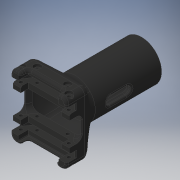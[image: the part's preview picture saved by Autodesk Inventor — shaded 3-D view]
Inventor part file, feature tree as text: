
AUTODESK INVENTOR PART (.ipt)
format: ipt  version: 2019 (Build 230136000, 136)  size: 1,152,512 bytes
history: native  units: in
note: dims shown in document units (in); Inventor stores cm internally (conversion verified against a paired STEP export)
features: extrude x9, sketch x7, chamfer x4, other x3, plane x3, fillet x2, loft x2, shell x1, pattern_circular x1, emboss x1, projected_geometry x1
ambient origin geometry x8: Origin, YZ Plane, XZ Plane, XY Plane, X Axis, Y Axis, Z Axis, Center Point
bodies: Solid3 (feature_tree), Solid1 (feature_tree)
feature tree (34):
  other  "servo holder.ipt"
  plane  "Work Plane2"
  extrude  "Extrusion2"  Depth=0.3937in
  fillet  "Fillet1"  Radius=1.1417in
  plane  "Work Plane1"
  sketch  "Sketch1"  dims[d0=0.3937in d1=2.4283in d2=1.1417in]
  sketch  "Sketch2"  dims[d7=0.9449in d8=0.0787in]
  extrude  "Extrusion8"  Depth=0.0787in
  loft  "Loft2"
  shell  "Shell1"  Thickness=0.0787in
  loft  "Loft3"
  extrude  "Extrusion1"  Depth=0.1969in
  sketch  "Sketch4"  dims[d21=0.0in d22=0.0in d23=0.0689in]
  extrude  "Extrusion3"  Depth=0.7874in TaperAngle=0.0deg
  extrude  "Extrusion4"  Depth=0.2362in TaperAngle=0.0deg
  extrude  "Extrusion5"  Depth=0.1575in
  chamfer  "Chamfer2"  Distance=3.1496in Angle=360.0deg
  pattern_circular  "Circular Pattern1"  [2 undecoded]
  extrude  "Extrusion6"  Depth=0.4331in
  chamfer  "Chamfer1"  Distance=0.1969in Angle=45.0deg
  plane  "Work Plane3"
  sketch  "Sketch5"  dims[d29=0.1102in d35=0.1969in]
  extrude  "Extrusion7"  Depth=0.1575in TaperAngle=45.0deg
  emboss  "Emboss1"
  fillet  "Fillet2"  Radius=0.3937in
  chamfer  "Chamfer3"  Distance=0.4724in
  extrude  "Extrusion9"  Depth=0.2362in
  chamfer  "Chamfer4"  Distance=0.2362in
  other  "Solid1::servo holder.ipt"
  other  "TaggingFeature1"
  sketch  "Sketch3"  dims[d11=0.3937in d12=90.0deg d13=1.1811in d14=90.0deg d15=0.1969in d16=90.0deg d17=0.1575in d18=0.0in d19=2.3622in d20=0.0787in]
  sketch  "Sketch6"  dims[d36=0.9843in d37=-0.0137in d38=0.7874in d39=0.0in]
  sketch  "Sketch7"  dims[d40=0.3937in d42=0.2362in d43=0.0in d44=0.1575in d45=3.1496in d46=360.0deg d48=0.2362in d49=0.0in d50=0.4331in d51=0.1969in d52=0.0787in d53=45.0deg d54=0.0394in d55=0.0787in d56=45.0deg d57=0.3937in d58=0.4724in d59=0.2362in d60=0.2362in d61=0.0in d62=0.0787in d63=0.0591in d64=0.0in d65=0.2756in d66=0.0295in d67=0.0394in d68=0.0787in d69=1.8898in d70=0.0in d73=0.3937in d74=90.0deg d75=0.1181in d76=0.0787in d77=45.0deg d78=0.0591in d79=0.0591in d80=0.0591in d81=0.0in d82=0.1575in d83=0.0787in d84=0.0935in d85=0.1575in d86=0.0787in d87=0.1575in d88=0.1575in d89=0.0591in d90=0.0787in d91=45.0deg]
  projected_geometry  "Projected Loop1"
note: 2 required parameter values undecoded (feature->parameter linkage not recoverable at this tier; creation-order binding heuristic only, values carry confidence <= 0.55)
